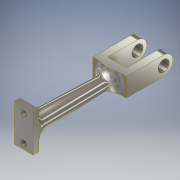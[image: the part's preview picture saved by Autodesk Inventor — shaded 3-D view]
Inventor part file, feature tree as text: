
AUTODESK INVENTOR PART (.ipt)
format: ipt  version: 2017 (Build 210142000, 142)  size: 244,224 bytes
history: native  units: mm
features: sketch x8, extrude x6, plane x3, fillet x3, loft x1
ambient origin geometry x8: Origin, YZ Plane, XZ Plane, XY Plane, X Axis, Y Axis, Z Axis, Center Point
bodies: Solid1 (feature_tree)
feature tree (21):
  sketch  "Sketch1"  dims[d0=9.5mm d1=43.0mm d2=6.5mm]
  plane  "Work Plane1"
  loft  "Loft1"
  extrude  "Extrusion1"  TaperAngle=0.0deg  [1 undecoded]
  extrude  "Extrusion2"  Depth=3.0mm TaperAngle=0.0deg
  extrude  "Extrusion3"  Depth=3.0mm
  fillet  "Fillet1"  [1 undecoded]
  extrude  "Extrusion5"  Depth=5.0mm
  fillet  "Fillet4"  Radius=5.0mm
  sketch  "Sketch10"  dims[d35=0.0mm d36=5.0mm d37=0.0mm]
  plane  "Work Plane3"
  plane  "Work Plane2"
  extrude  "Extrusion10"  Depth=5.0mm
  fillet  "Fillet6"  [1 undecoded]
  extrude  "Extrusion11"  TaperAngle=0.0deg  [1 undecoded]
  sketch  "Sketch2"  dims[d3=0.0mm d4=90.0deg d5=0.0mm d6=90.0deg]
  sketch  "Sketch3"  dims[d7=5.0mm d8=10.0mm d9=10.0mm d10=20.0mm d11=10.0mm d12=3.0mm d13=0.0mm]
  sketch  "Sketch4"  dims[d14=10.0mm d15=3.0mm d16=0.0mm]
  sketch  "Sketch5"  dims[d17=3.0mm d18=14.0mm d19=3.0mm d20=3.0mm d21=5.0mm d22=0.0mm d29=3.0mm d31=0.0mm]
  sketch  "Sketch7"  dims[d32=0.0mm d33=9.5mm d34=5.0mm]
  sketch  "Sketch12"  dims[d38=0.0mm d39=0.0mm d40=10.0mm d41=5.0mm d42=0.0mm d43=10.0mm d61=4.0mm d62=0.0mm d71=5.0mm d79=10.0mm d80=4.5mm d81=10.0mm d82=14.0mm d83=18.0mm d84=9.0mm d85=4.0mm d86=9.0mm d87=9.0mm d97=0.59mm d102=10.045mm d103=90.0deg d105=90.0deg d106=2.07063mm d108=18.0mm d109=18.0mm d110=21.0mm d111=0.0mm d112=5.0mm d113=6.0mm d114=21.0mm d115=0.0mm]
note: 4 required parameter values undecoded (feature->parameter linkage not recoverable at this tier; creation-order binding heuristic only, values carry confidence <= 0.55)
